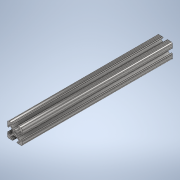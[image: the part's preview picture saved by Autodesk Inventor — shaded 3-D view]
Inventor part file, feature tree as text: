
AUTODESK INVENTOR PART (.ipt)
format: ipt  version: 2020 (Build 240168000, 168)  size: 238,592 bytes
history: native  units: in
note: dims shown in document units (in); Inventor stores cm internally (conversion verified against a paired STEP export)
features: extrude x1, sketch x1
ambient origin geometry x8: Origin, YZ Plane, XZ Plane, XY Plane, X Axis, Y Axis, Z Axis, Center Point
bodies: Solid1 (feature_tree)
feature tree (2):
  extrude  "Extrusion1"  [1 undecoded]
  sketch  "Sketch1"  dims[d0=10.0in d1=0.0in]
note: 1 required parameter value undecoded (feature->parameter linkage not recoverable at this tier; creation-order binding heuristic only, values carry confidence <= 0.55)
